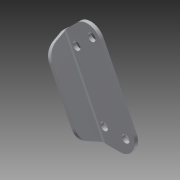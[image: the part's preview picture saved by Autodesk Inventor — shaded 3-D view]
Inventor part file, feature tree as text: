
AUTODESK INVENTOR PART (.ipt)
format: ipt  version: 2014 SP1 (Build 180222100, 222)  size: 240,640 bytes
history: native  units: in
note: dims shown in document units (in); Inventor stores cm internally (conversion verified against a paired STEP export)
features: reference x4, sheet_metal_op x2, other x2, sketch x1, chamfer x1
ambient origin geometry x8: Origin, YZ Plane, XZ Plane, XY Plane, X Axis, Y Axis, Z Axis, Center Point
bodies: Solid1 (feature_tree)
feature tree (10):
  sketch  "Sketch1"  dims[d0=0.5in d1=0.25in d2=1.0in d5=0.75in d6=0.125in d7=0.125in d8=0.0625in d9=0.25in d10=0.125in d11=90.0deg d12=0.05in d13=0.5in d14=0.5in d15=0.25in d16=0.1in d17=0.25in d18=3.0503in d19=1.5748in d21=0.7668in d22=0.3937in d24=1.0in]
  sheet_metal_op  "Face1"
  sheet_metal_op  "Fold1"
  chamfer  "Corner Round1"
  reference  "Reference2"
  reference  "Reference3"
  other  "Plate1"
  reference  "Reference6"
  reference  "Reference7"
  other  "Definition1"
